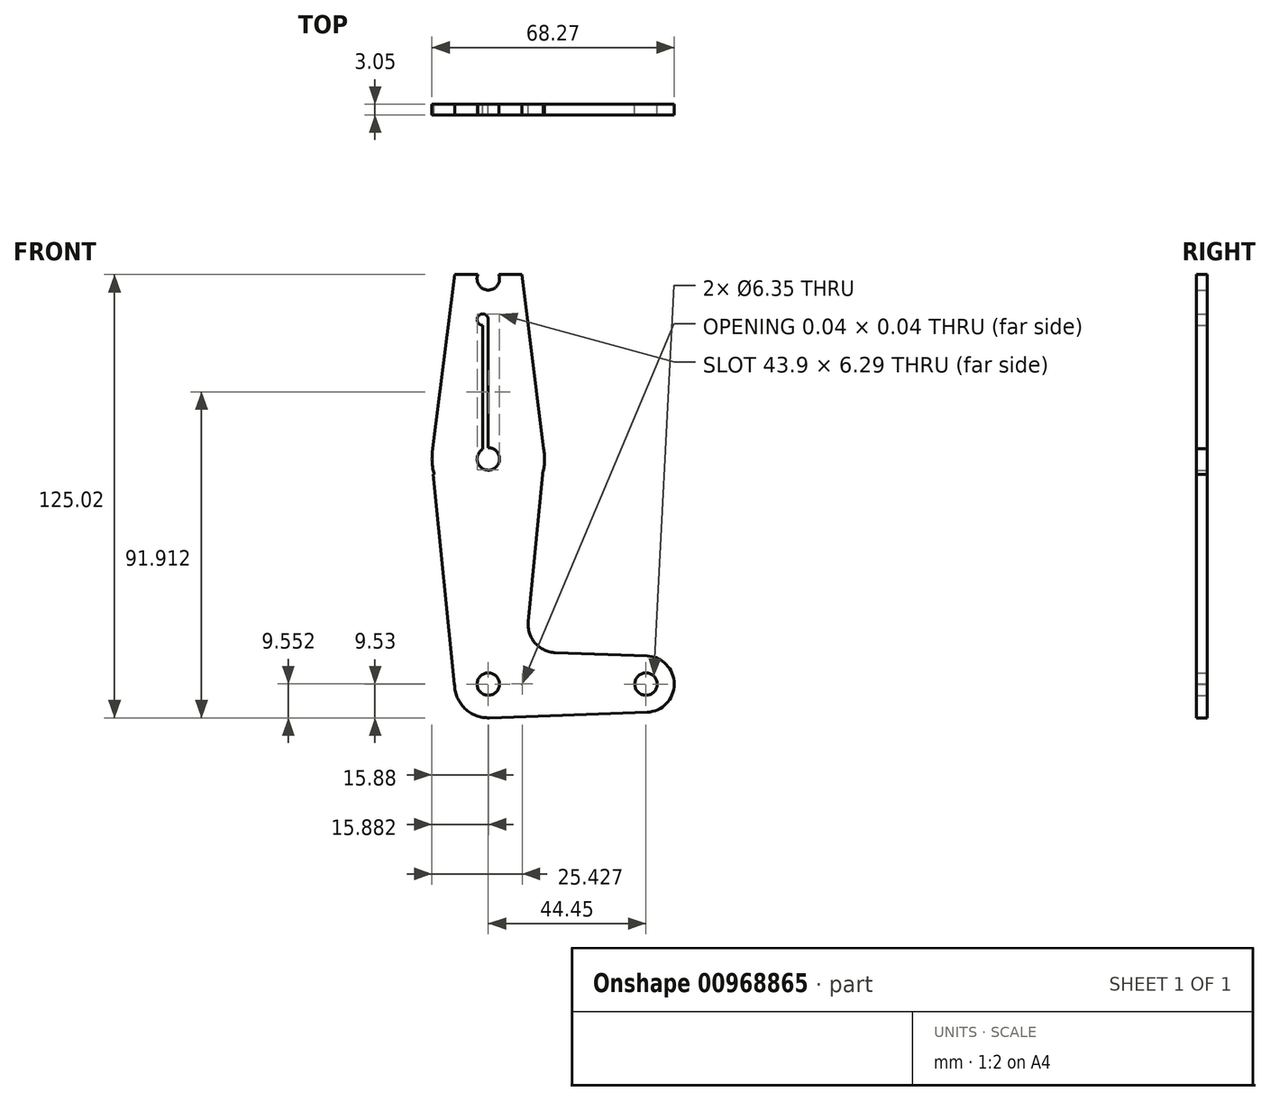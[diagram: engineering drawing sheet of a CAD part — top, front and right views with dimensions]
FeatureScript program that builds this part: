
annotation { "Feature Type Name" : "Feature", "Feature Type Description" : "" }
export const myFeature = defineFeature(function(context is Context, id is Id, definition is map)
    precondition{}
    {
        {
            var Q0;
            Q0=qCreatedBy(makeId("Front.planeOp"),FACE);
            var sketch = newSketch(context, id + "F0", { "sketchPlane" : qUnion([Q0])});
            skCircle(sketch, "E0", {"center": v(0, 0) * mm, "radius": 9.53 * mm});
            skCircle(sketch, "E1", {"center": v(0, 63.5) * mm, "radius": 15.88 * mm});
            skCircle(sketch, "E2", {"center": v(0, 114.3) * mm, "radius": 9.53 * mm});
            skCircle(sketch, "E3", {"center": v(44.45, 0) * mm, "radius": 7.94 * mm});
            skLineSegment(sketch, "E4", {"start": v(0, 0) * mm, "end": v(0, 114.3) * mm});
            skLineSegment(sketch, "E5", {"start": v(0, 63.5) * mm, "end": v(0, 0) * mm, "construction": true});
            skLineSegment(sketch, "E6", {"start": v(0, 0) * mm, "end": v(44.45, 0) * mm});
            skLineSegment(sketch, "E7", {"start": v(15.84, 64.51) * mm, "end": v(9.45, 115.49) * mm});
            skLineSegment(sketch, "E8", {"start": v(9.45, 115.49) * mm, "end": v(-9.45, 115.49) * mm});
            skLineSegment(sketch, "E9", {"start": v(-9.45, 115.49) * mm, "end": v(-15.75, 65.48) * mm});
            skLineSegment(sketch, "E10", {"start": v(-9.52, 0) * mm, "end": v(-15.5, 59.08) * mm});
            skLineSegment(sketch, "E11", {"start": v(-15.5, 59.08) * mm, "end": v(15.25, 59.08) * mm});
            skLineSegment(sketch, "E12", {"start": v(15.25, 59.08) * mm, "end": v(11.26, 17.56) * mm});
            skLineSegment(sketch, "E13", {"start": v(9.57, 0) * mm, "end": v(0, 9.53) * mm});
            skLineSegment(sketch, "E14", {"start": v(18.89, 8.85) * mm, "end": v(44.73, 7.93) * mm});
            skLineSegment(sketch, "E15", {"start": v(44.73, 7.93) * mm, "end": v(44.73, -7.93) * mm});
            skLineSegment(sketch, "E16", {"start": v(44.73, -7.93) * mm, "end": v(0, -9.53) * mm});
            skCircle(sketch, "E17", {"center": v(0, 114.3) * mm, "radius": 3.18 * mm});
            skCircle(sketch, "E18", {"center": v(0, 63.5) * mm, "radius": 3.18 * mm});
            skCircle(sketch, "E19", {"center": v(0, 0) * mm, "radius": 3.18 * mm});
            skCircle(sketch, "E20", {"center": v(44.45, 0) * mm, "radius": 3.18 * mm});
            skCircle(sketch, "E21", {"center": v(-1.59, 102.77) * mm, "radius": 1.59 * mm});
            skLineSegment(sketch, "E22", {"start": v(-1.59, 102.77) * mm, "end": v(-1.59, 66.25) * mm});
            skArc(sketch, "E23.filletArc", {"start": v(11.26, 17.56) * mm, "mid": v(13.2, 11.56) * mm, "end": v(18.89, 8.85) * mm});
            skSolve(sketch);
        }
        {
            var Q0;
            {var subQ0=sQuery(id+"F0.wireOp",EDGE,"E4");var subQ1=sQuery(id+"F0.wireOp",EDGE,"E1");var subQ2=makeQuery(id+"F0.imprint","INTERSECT",VERTEX,{"disambiguationData":[OD(0.0)],"derivedFrom":[subQ1,subQ0]});Q0=makeQuery(id+"F0.imprint","IMPRINT",FACE,{"disambiguationData":[TD([[makeQuery(id+"F0.imprint","IMPRINT",EDGE,{"disambiguationData":[TD([[subQ2,-1.0]])],"derivedFrom":subQ1}),-1.0]])]});}
            var Q1;
            {var subQ0=sQuery(id+"F0.wireOp",EDGE,"E7");var subQ1=sQuery(id+"F0.wireOp",EDGE,"E1");var subQ2=makeQuery(id+"F0.imprint","INTERSECT",VERTEX,{"disambiguationData":[OD(0.0)],"derivedFrom":[subQ1,subQ0]});Q1=makeQuery(id+"F0.imprint","IMPRINT",FACE,{"disambiguationData":[TD([[makeQuery(id+"F0.imprint","IMPRINT",EDGE,{"disambiguationData":[TD([[subQ2,-1.0]])],"derivedFrom":subQ1}),1.0]])]});}
            var Q2;
            {var subQ7=sQuery(id+"F0.wireOp",EDGE,"E10");Q2=makeQuery(id+"F0.imprint","IMPRINT",FACE,{"disambiguationData":[TD([[makeQuery(id+"F0.imprint","IMPRINT",EDGE,{"derivedFrom":subQ7}),-1.0]])]});}
            var Q3;
            {var subQ0=sQuery(id+"F0.wireOp",EDGE,"E11");var subQ1=sQuery(id+"F0.wireOp",EDGE,"E1");var subQ2=makeQuery(id+"F0.imprint","INTERSECT",VERTEX,{"derivedFrom":[subQ1,subQ0]});Q3=makeQuery(id+"F0.imprint","IMPRINT",FACE,{"disambiguationData":[TD([[makeQuery(id+"F0.imprint","IMPRINT",EDGE,{"disambiguationData":[TD([[subQ2,-1.0]])],"derivedFrom":subQ1}),1.0]])]});}
            var Q4;
            {var subQ1=sQuery(id+"F0.wireOp",EDGE,"E1");var subQ3=sQuery(id+"F0.wireOp",EDGE,"E4");var subQ4=makeQuery(id+"F0.imprint","INTERSECT",VERTEX,{"disambiguationData":[OD(1.0)],"derivedFrom":[subQ1,subQ3]});Q4=makeQuery(id+"F0.imprint","IMPRINT",FACE,{"disambiguationData":[TD([[makeQuery(id+"F0.imprint","IMPRINT",EDGE,{"disambiguationData":[TD([[subQ4,-1.0]])],"derivedFrom":subQ3}),-1.0]])]});}
            var Q5;
            {var subQ0=sQuery(id+"F0.wireOp",EDGE,"E8");var subQ4=sQuery(id+"F0.wireOp",EDGE,"E17");var subQ6=makeQuery(id+"F0.imprint","INTERSECT",VERTEX,{"disambiguationData":[OD(0.0)],"derivedFrom":[subQ0,subQ4]});Q5=makeQuery(id+"F0.imprint","IMPRINT",FACE,{"disambiguationData":[TD([[makeQuery(id+"F0.imprint","IMPRINT",EDGE,{"disambiguationData":[TD([[subQ6,-1.0]])],"derivedFrom":subQ4}),-1.0]])]});}
            var Q6;
            {var subQ0=sQuery(id+"F0.wireOp",EDGE,"E15");var subQ4=sQuery(id+"F0.wireOp",EDGE,"E20");var subQ5=makeQuery(id+"F0.imprint","INTERSECT",VERTEX,{"disambiguationData":[OD(0.0)],"derivedFrom":[subQ0,subQ4]});Q6=makeQuery(id+"F0.imprint","IMPRINT",FACE,{"disambiguationData":[TD([[makeQuery(id+"F0.imprint","IMPRINT",EDGE,{"disambiguationData":[TD([[subQ5,1.0]])],"derivedFrom":subQ4}),-1.0]])]});}
            var Q7;
            {var subQ1=sQuery(id+"F0.wireOp",EDGE,"E0");var subQ9=makeQuery(id+"F0.imprint","INTERSECT",VERTEX,{"derivedFrom":[subQ1,sQuery(id+"F0.wireOp",EDGE,"E10")]});Q7=makeQuery(id+"F0.imprint","IMPRINT",FACE,{"disambiguationData":[TD([[makeQuery(id+"F0.imprint","IMPRINT",EDGE,{"disambiguationData":[TD([[subQ9,-1.0]])],"derivedFrom":subQ1}),1.0]])]});}
            var Q8;
            {var subQ2=sQuery(id+"F0.wireOp",EDGE,"E0");var subQ6=sQuery(id+"F0.wireOp",EDGE,"E16");var subQ8=makeQuery(id+"F0.imprint","INTERSECT",VERTEX,{"derivedFrom":[subQ2,subQ6]});Q8=makeQuery(id+"F0.imprint","IMPRINT",FACE,{"disambiguationData":[TD([[makeQuery(id+"F0.imprint","IMPRINT",EDGE,{"disambiguationData":[TD([[subQ8,-1.0]])],"derivedFrom":subQ2}),-1.0]])]});}
            var Q9;
            {var subQ4=sQuery(id+"F0.wireOp",EDGE,"E7");var subQ6=sQuery(id+"F0.wireOp",EDGE,"E1");var subQ8=makeQuery(id+"F0.imprint","INTERSECT",VERTEX,{"disambiguationData":[OD(1.0)],"derivedFrom":[subQ6,subQ4]});Q9=makeQuery(id+"F0.imprint","IMPRINT",FACE,{"disambiguationData":[TD([[makeQuery(id+"F0.imprint","IMPRINT",EDGE,{"disambiguationData":[TD([[subQ8,-1.0]])],"derivedFrom":subQ6}),-1.0]])]});}
            var Q10;
            {var subQ3=sQuery(id+"F0.wireOp",EDGE,"E4");var subQ5=sQuery(id+"F0.wireOp",EDGE,"E17");var subQ6=makeQuery(id+"F0.imprint","INTERSECT",VERTEX,{"derivedFrom":[subQ3,subQ5]});Q10=makeQuery(id+"F0.imprint","IMPRINT",FACE,{"disambiguationData":[TD([[makeQuery(id+"F0.imprint","IMPRINT",EDGE,{"disambiguationData":[TD([[subQ6,1.0]])],"derivedFrom":subQ3}),1.0]])]});}
            var Q11;
            {var subQ3=sQuery(id+"F0.wireOp",EDGE,"E6");var subQ5=sQuery(id+"F0.wireOp",EDGE,"E20");var subQ6=makeQuery(id+"F0.imprint","INTERSECT",VERTEX,{"derivedFrom":[subQ3,subQ5]});Q11=makeQuery(id+"F0.imprint","IMPRINT",FACE,{"disambiguationData":[TD([[makeQuery(id+"F0.imprint","IMPRINT",EDGE,{"disambiguationData":[TD([[subQ6,1.0]])],"derivedFrom":subQ3}),1.0]])]});}
            var Q12;
            {var subQ3=sQuery(id+"F0.wireOp",EDGE,"E6");var subQ5=sQuery(id+"F0.wireOp",EDGE,"E20");var subQ6=makeQuery(id+"F0.imprint","INTERSECT",VERTEX,{"derivedFrom":[subQ3,subQ5]});Q12=makeQuery(id+"F0.imprint","IMPRINT",FACE,{"disambiguationData":[TD([[makeQuery(id+"F0.imprint","IMPRINT",EDGE,{"disambiguationData":[TD([[subQ6,1.0]])],"derivedFrom":subQ3}),-1.0]])]});}
            var Q13;
            {var subQ1=sQuery(id+"F0.wireOp",EDGE,"E1");var subQ5=makeQuery(id+"F0.imprint","INTERSECT",VERTEX,{"derivedFrom":[subQ1,sQuery(id+"F0.wireOp",EDGE,"E9")]});Q13=makeQuery(id+"F0.imprint","IMPRINT",FACE,{"disambiguationData":[TD([[makeQuery(id+"F0.imprint","IMPRINT",EDGE,{"disambiguationData":[TD([[subQ5,1.0]])],"derivedFrom":subQ1}),1.0]])]});}
            var Q14;
            {var subQ5=sQuery(id+"F0.wireOp",EDGE,"E9");Q14=makeQuery(id+"F0.imprint","IMPRINT",FACE,{"disambiguationData":[TD([[makeQuery(id+"F0.imprint","IMPRINT",EDGE,{"derivedFrom":subQ5}),1.0]])]});}
            var Q15;
            {var subQ11=sQuery(id+"F0.wireOp",EDGE,"E12");Q15=makeQuery(id+"F0.imprint","IMPRINT",FACE,{"disambiguationData":[TD([[makeQuery(id+"F0.imprint","IMPRINT",EDGE,{"derivedFrom":subQ11}),-1.0]])]});}
            var Q16;
            {var subQ1=sQuery(id+"F0.wireOp",EDGE,"E1");var subQ8=sQuery(id+"F0.wireOp",EDGE,"E7");var subQ11=makeQuery(id+"F0.imprint","INTERSECT",VERTEX,{"disambiguationData":[OD(1.0)],"derivedFrom":[subQ1,subQ8]});Q16=makeQuery(id+"F0.imprint","IMPRINT",FACE,{"disambiguationData":[TD([[makeQuery(id+"F0.imprint","IMPRINT",EDGE,{"disambiguationData":[TD([[subQ11,-1.0]])],"derivedFrom":subQ1}),1.0]])]});}
            var Q17;
            {var subQ0=sQuery(id+"F0.wireOp",EDGE,"E4");var subQ1=sQuery(id+"F0.wireOp",EDGE,"E1");var subQ2=makeQuery(id+"F0.imprint","INTERSECT",VERTEX,{"disambiguationData":[OD(0.0)],"derivedFrom":[subQ1,subQ0]});Q17=makeQuery(id+"F0.imprint","IMPRINT",FACE,{"disambiguationData":[TD([[makeQuery(id+"F0.imprint","IMPRINT",EDGE,{"disambiguationData":[TD([[subQ2,-1.0]])],"derivedFrom":subQ1}),1.0]])]});}
            var Q18;
            {var subQ0=sQuery(id+"F0.wireOp",EDGE,"E13");var subQ1=sQuery(id+"F0.wireOp",EDGE,"E0");var subQ3=makeQuery(id+"F0.imprint","INTERSECT",VERTEX,{"derivedFrom":[subQ1,subQ0]});Q18=makeQuery(id+"F0.imprint","IMPRINT",FACE,{"disambiguationData":[TD([[makeQuery(id+"F0.imprint","IMPRINT",EDGE,{"disambiguationData":[TD([[subQ3,-1.0]])],"derivedFrom":subQ1}),1.0]])]});}
            var Q19;
            {var subQ0=sQuery(id+"F0.wireOp",EDGE,"E13");var subQ2=sQuery(id+"F0.wireOp",EDGE,"E0");var subQ4=makeQuery(id+"F0.imprint","INTERSECT",VERTEX,{"derivedFrom":[subQ2,subQ0]});Q19=makeQuery(id+"F0.imprint","IMPRINT",FACE,{"disambiguationData":[TD([[makeQuery(id+"F0.imprint","IMPRINT",EDGE,{"disambiguationData":[TD([[subQ4,1.0]])],"derivedFrom":subQ2}),1.0]])]});}
            var Q20;
            {var subQ3=sQuery(id+"F0.wireOp",EDGE,"E4");var subQ5=sQuery(id+"F0.wireOp",EDGE,"E17");var subQ6=makeQuery(id+"F0.imprint","INTERSECT",VERTEX,{"derivedFrom":[subQ3,subQ5]});Q20=makeQuery(id+"F0.imprint","IMPRINT",FACE,{"disambiguationData":[TD([[makeQuery(id+"F0.imprint","IMPRINT",EDGE,{"disambiguationData":[TD([[subQ6,1.0]])],"derivedFrom":subQ3}),-1.0]])]});}
            extrude(context, id + "F1", {"entities" : qUnion([Q0, Q1, Q2, Q3, Q4, Q5, Q6, Q7, Q8, Q9, Q10, Q11, Q12, Q13, Q14, Q15, Q16, Q17, Q18, Q19, Q20]), "depth" : 3.05 * mm, "offsetDistance" : 25.4 * mm});
        }
    });
